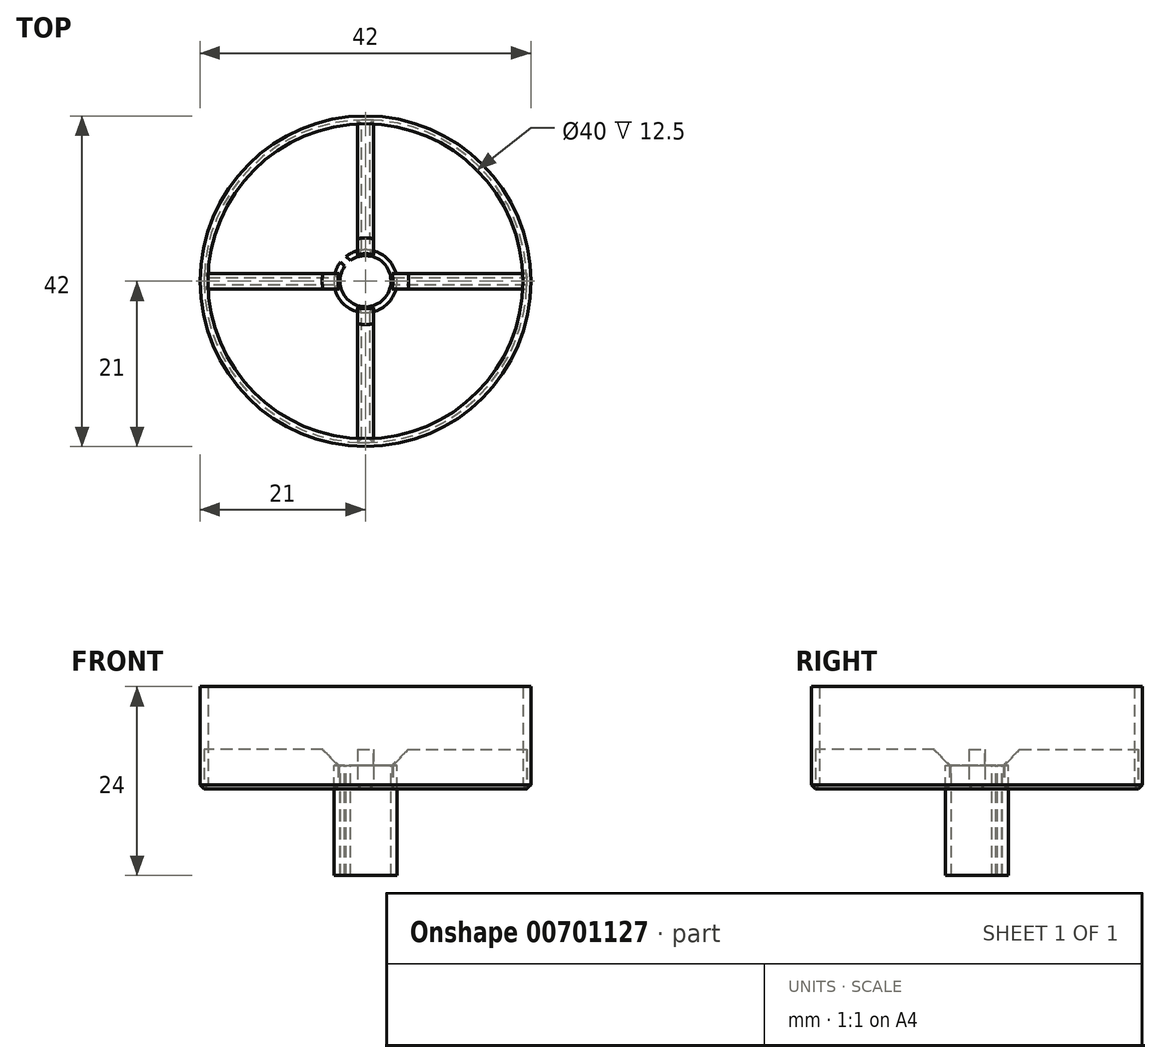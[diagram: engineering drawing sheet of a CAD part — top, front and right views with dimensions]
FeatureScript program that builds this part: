
annotation { "Feature Type Name" : "Feature", "Feature Type Description" : "" }
export const myFeature = defineFeature(function(context is Context, id is Id, definition is map)
    precondition{}
    {
        {
            var Q0;
            Q0=qCreatedBy(makeId("Top.planeOp"),FACE);
            var sketch = newSketch(context, id + "F0", { "sketchPlane" : qUnion([Q0])});
            skCircle(sketch, "E0", {"center": v(0, 0) * mm, "radius": 20 * mm});
            skCircle(sketch, "E1", {"center": v(0, 0) * mm, "radius": 21 * mm});
            skSolve(sketch);
        }
        {
            var Q0;
            Q0 = qSketchRegion(id + "F0", true);
            extrude(context, id + "F1", {"entities" : qUnion([Q0]), "depth" : 10 * mm, "offsetDistance" : 25 * mm, "hasSecondDirection" : true, "secondDirectionOppositeDirection" : true, "secondDirectionDepth" : 3 * mm});
        }
        {
            var Q0;
            Q0=qCreatedBy(makeId("Top.planeOp"),FACE);
            var sketch = newSketch(context, id + "F2", { "sketchPlane" : qUnion([Q0])});
            skCircle(sketch, "E2", {"center": v(0, 0) * mm, "radius": 3.25 * mm});
            skCircle(sketch, "E3", {"center": v(0, 0) * mm, "radius": 4 * mm});
            skSolve(sketch);
        }
        {
            var Q0;
            Q0=makeQuery(id+"F2.imprint","IMPRINT",FACE,{"disambiguationData":[TD([[makeQuery(id+"F2.imprint","IMPRINT",EDGE,{"derivedFrom":sQuery(id+"F2.wireOp",EDGE,"E2")}),-1.0]])]});
            var Q1;
            Q1=sQuery(id+"F2.wireOp",EDGE,"E2");
            var Q2;
            Q2=sQuery(id+"F2.wireOp",EDGE,"E3");
            extrude(context, id + "F3", {"entities" : qUnion([Q0]), "surfaceEntities" : qUnion([Q1, Q2]), "oppositeDirection" : true, "depth" : 14 * mm, "offsetDistance" : 25 * mm});
        }
        {
            var Q0;
            Q0=qCreatedBy(makeId("Top.planeOp"),FACE);
            var sketch = newSketch(context, id + "F4", { "sketchPlane" : qUnion([Q0])});
            skLineSegment(sketch, "E4.0", {"start": v(3.35, -1) * mm, "end": v(20.48, -1) * mm});
            skArc(sketch, "E5", {"start": v(-1, -3.35) * mm, "mid": v(0, -3.5) * mm, "end": v(1, -3.35) * mm});
            skArc(sketch, "E6", {"start": v(20.48, -1) * mm, "mid": v(20.5, 0) * mm, "end": v(20.48, 1) * mm});
            skLineSegment(sketch, "E7.trimOffspring", {"start": v(-3.35, -1) * mm, "end": v(-20.48, -1) * mm});
            skLineSegment(sketch, "E8.trimOffspring", {"start": v(-3.35, 1) * mm, "end": v(-20.48, 1) * mm});
            skLineSegment(sketch, "E9.trimOffspring", {"start": v(1, -3.35) * mm, "end": v(1, -20.48) * mm});
            skLineSegment(sketch, "E10.trimOffspring", {"start": v(-1, -3.35) * mm, "end": v(-1, -20.48) * mm});
            skArc(sketch, "E11.trimOffspring", {"start": v(-3.35, 1) * mm, "mid": v(-3.5, 0) * mm, "end": v(-3.35, -1) * mm});
            skArc(sketch, "E12.trimOffspring", {"start": v(1, 3.35) * mm, "mid": v(0, 3.5) * mm, "end": v(-1, 3.35) * mm});
            skArc(sketch, "E13.trimOffspring", {"start": v(3.35, -1) * mm, "mid": v(3.5, 0) * mm, "end": v(3.35, 1) * mm});
            skLineSegment(sketch, "E14.trimOffspring", {"start": v(3.35, 1) * mm, "end": v(20.48, 1) * mm});
            skLineSegment(sketch, "E15.trimOffspring", {"start": v(1, 3.35) * mm, "end": v(1, 20.48) * mm});
            skLineSegment(sketch, "E16.trimOffspring", {"start": v(-1, 3.35) * mm, "end": v(-1, 20.48) * mm});
            skArc(sketch, "E17.trimOffspring", {"start": v(-1, -20.48) * mm, "mid": v(0, -20.5) * mm, "end": v(1, -20.48) * mm});
            skArc(sketch, "E18.trimOffspring", {"start": v(1, 20.48) * mm, "mid": v(0, 20.5) * mm, "end": v(-1, 20.48) * mm});
            skArc(sketch, "E19.trimOffspring", {"start": v(-20.48, 1) * mm, "mid": v(-20.5, 0) * mm, "end": v(-20.48, -1) * mm});
            skSolve(sketch);
        }
        {
            var Q0;
            Q0 = qSketchRegion(id + "F4", true);
            extrude(context, id + "F5", {"entities" : qUnion([Q0]), "depth" : 2 * mm, "offsetDistance" : 25 * mm, "hasSecondDirection" : true, "secondDirectionOppositeDirection" : true, "secondDirectionDepth" : 3 * mm});
        }
        {
            var Q0;
            Q0=makeQuery(id+"F5.opExtrude","CAP_EDGE",EDGE,{"disambiguationData":[OSD([sQuery(id+"F4.wireOp",EDGE,"E12.trimOffspring")])],"isStart":false});
            var Q1;
            Q1=makeQuery(id+"F5.opExtrude","CAP_EDGE",EDGE,{"disambiguationData":[OSD([sQuery(id+"F4.wireOp",EDGE,"E13.trimOffspring")])],"isStart":false});
            var Q2;
            Q2=makeQuery(id+"F5.opExtrude","CAP_EDGE",EDGE,{"disambiguationData":[OSD([sQuery(id+"F4.wireOp",EDGE,"E5")])],"isStart":false});
            var Q3;
            Q3=makeQuery(id+"F5.opExtrude","CAP_EDGE",EDGE,{"disambiguationData":[OSD([sQuery(id+"F4.wireOp",EDGE,"E11.trimOffspring")])],"isStart":false});
            chamfer(context, id + "F6", {"entities" : qUnion([Q0, Q1, Q2, Q3]), "width" : 2 * mm, "tangentPropagation" : true});
        }
        {
            var Q0;
            Q0=qCreatedBy(makeId("Top.planeOp"),FACE);
            var sketch = newSketch(context, id + "F7", { "sketchPlane" : qUnion([Q0])});
            skLineSegment(sketch, "E20.0", {"start": v(-3.17, 2.44) * mm, "end": v(-2.46, 1.72) * mm});
            skLineSegment(sketch, "E21.0", {"start": v(-2.45, 3.16) * mm, "end": v(-1.74, 2.45) * mm});
            skArc(sketch, "E22", {"start": v(-1.74, 2.45) * mm, "mid": v(-2.13, 2.11) * mm, "end": v(-2.46, 1.72) * mm});
            skArc(sketch, "E23", {"start": v(-2.45, 3.16) * mm, "mid": v(-2.84, 2.82) * mm, "end": v(-3.17, 2.44) * mm});
            skSolve(sketch);
        }
        {
            var Q0;
            Q0=makeQuery(id+"F7.imprint","IMPRINT",FACE,{"disambiguationData":[TD([[makeQuery(id+"F7.imprint","IMPRINT",EDGE,{"derivedFrom":sQuery(id+"F7.wireOp",EDGE,"E20.0")}),1.0]])]});
            var Q1;
            Q1=sQuery(id+"F7.wireOp",EDGE,"E22");
            var Q2;
            Q2=sQuery(id+"F7.wireOp",EDGE,"E21.0");
            var Q3;
            Q3=sQuery(id+"F7.wireOp",EDGE,"E20.0");
            var Q4;
            Q4=sQuery(id+"F7.wireOp",EDGE,"E23");
            var Q5;
            Q5=sQuery(id+"F7.wireOp",EDGE,"E22");
            extrude(context, id + "F8", {"entities" : qUnion([Q0]), "operationType" : NewBodyOperationType.REMOVE, "surfaceEntities" : qUnion([Q1, Q2, Q3, Q4, Q5]), "oppositeDirection" : true, "depth" : 15 * mm, "offsetDistance" : 25 * mm});
        }
        {
            var Q0;
            Q0=makeQuery(id+"F5.opExtrude","CAP_FACE",FACE,{"disambiguationData":[OSD([sQuery(id+"F4.wireOp",EDGE,"E5"),sQuery(id+"F4.wireOp",EDGE,"E9.trimOffspring"),sQuery(id+"F4.wireOp",EDGE,"E10.trimOffspring"),sQuery(id+"F4.wireOp",EDGE,"E17.trimOffspring")])],"isStart":true});
            var Q1;
            Q1=makeQuery(id+"F5.opExtrude","CAP_FACE",FACE,{"disambiguationData":[OSD([sQuery(id+"F4.wireOp",EDGE,"E12.trimOffspring"),sQuery(id+"F4.wireOp",EDGE,"E15.trimOffspring"),sQuery(id+"F4.wireOp",EDGE,"E16.trimOffspring"),sQuery(id+"F4.wireOp",EDGE,"E18.trimOffspring")])],"isStart":true});
            var Q2;
            Q2=makeQuery(id+"F5.opExtrude","CAP_FACE",FACE,{"disambiguationData":[OSD([sQuery(id+"F4.wireOp",EDGE,"E7.trimOffspring"),sQuery(id+"F4.wireOp",EDGE,"E8.trimOffspring"),sQuery(id+"F4.wireOp",EDGE,"E11.trimOffspring"),sQuery(id+"F4.wireOp",EDGE,"E19.trimOffspring")])],"isStart":true});
            var Q3;
            Q3=makeQuery(id+"F5.opExtrude","CAP_EDGE",EDGE,{"disambiguationData":[OSD([sQuery(id+"F4.wireOp",EDGE,"E14.trimOffspring")])],"isStart":true});
            var Q4;
            Q4=makeQuery(id+"F1.opExtrude","CAP_EDGE",EDGE,{"disambiguationData":[OSD([sQuery(id+"F0.wireOp",EDGE,"E1")])],"isStart":true});
            var Q5;
            Q5=makeQuery(id+"F1.opExtrude","CAP_EDGE",EDGE,{"disambiguationData":[OSD([sQuery(id+"F0.wireOp",EDGE,"E0")])],"isStart":true});
            var Q6;
            Q6=makeQuery(id+"F5.opExtrude","CAP_EDGE",EDGE,{"disambiguationData":[OSD([sQuery(id+"F4.wireOp",EDGE,"E4.0")])],"isStart":true});
            chamfer(context, id + "F9", {"entities" : qUnion([Q0, Q1, Q2, Q3, Q4, Q5, Q6]), "width" : .5 * mm, "tangentPropagation" : true});
        }
    });
